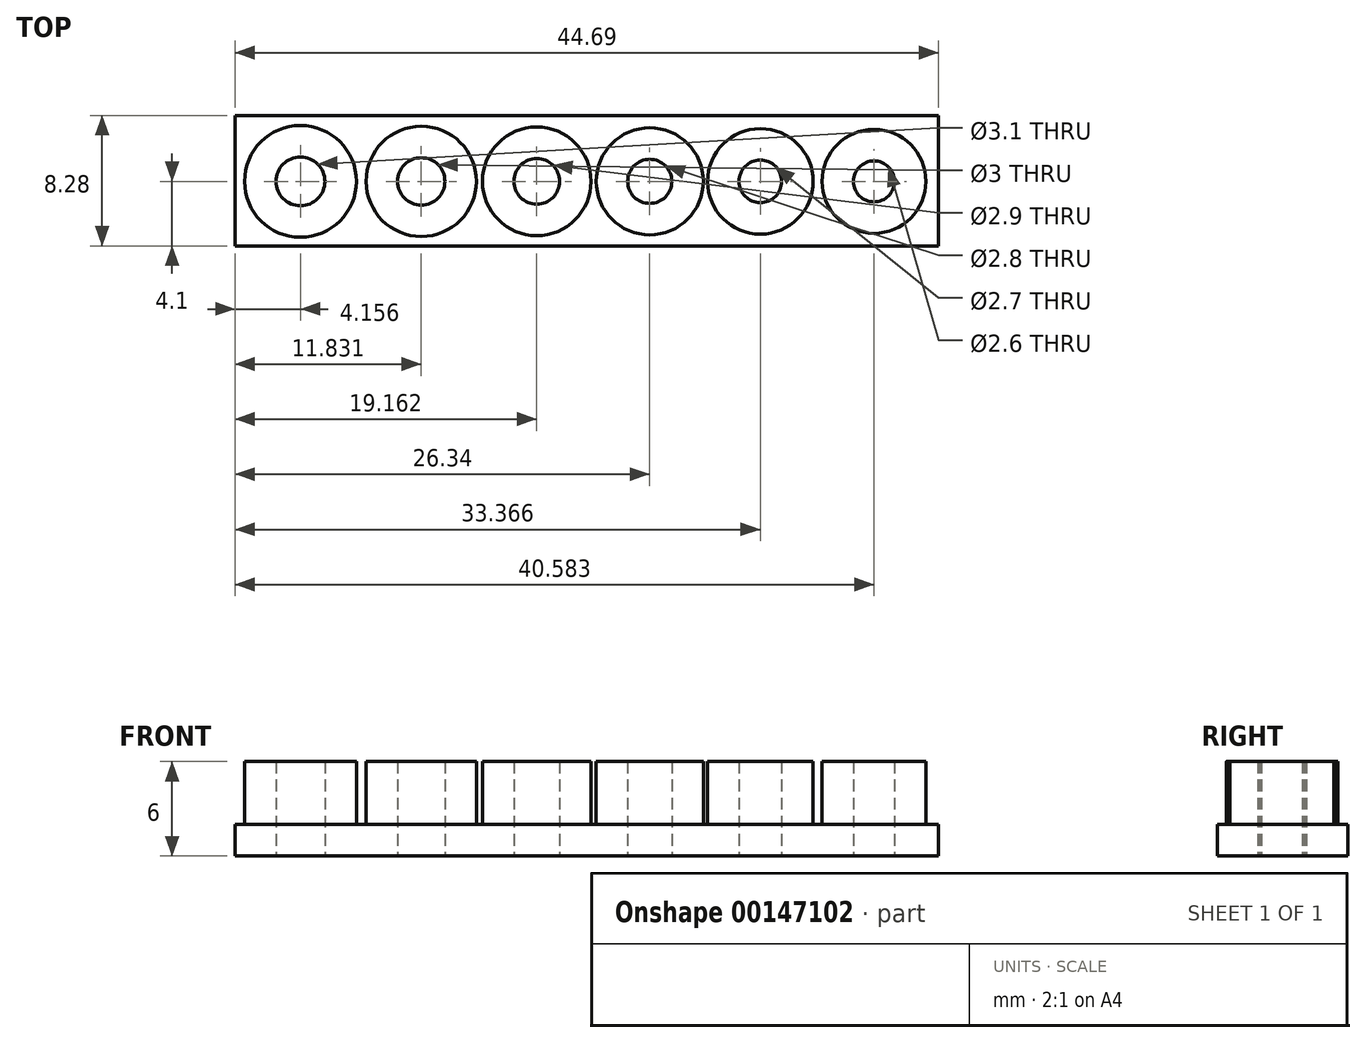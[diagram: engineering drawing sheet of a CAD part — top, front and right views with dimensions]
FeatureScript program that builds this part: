
annotation { "Feature Type Name" : "Feature", "Feature Type Description" : "" }
export const myFeature = defineFeature(function(context is Context, id is Id, definition is map)
    precondition{}
    {
        {
            var Q0;
            Q0=qCreatedBy(makeId("Top.planeOp"),FACE);
            var sketch = newSketch(context, id + "F0", { "sketchPlane" : qUnion([Q0])});
            skLineSegment(sketch, "E0", {"start": v(-20.66, -29) * mm, "end": v(15.04, -29) * mm, "construction": true});
            skCircle(sketch, "E1", {"center": v(-20.66, -29) * mm, "radius": 1.55 * mm});
            skCircle(sketch, "E2", {"center": v(-12.99, -29) * mm, "radius": 1.5 * mm});
            skCircle(sketch, "E3", {"center": v(-5.66, -29) * mm, "radius": 1.45 * mm});
            skCircle(sketch, "E4", {"center": v(1.52, -29) * mm, "radius": 1.4 * mm});
            skCircle(sketch, "E5", {"center": v(8.55, -29) * mm, "radius": 1.35 * mm});
            skCircle(sketch, "E6", {"center": v(15.76, -29) * mm, "radius": 1.3 * mm});
            skLineSegment(sketch, "E7.bottom", {"start": v(-24.82, -24.81) * mm, "end": v(19.87, -24.81) * mm});
            skLineSegment(sketch, "E7.top", {"start": v(-24.82, -33.1) * mm, "end": v(19.87, -33.1) * mm});
            skLineSegment(sketch, "E7.left", {"start": v(-24.82, -24.81) * mm, "end": v(-24.82, -33.1) * mm});
            skLineSegment(sketch, "E7.right", {"start": v(19.87, -24.81) * mm, "end": v(19.87, -33.1) * mm});
            skCircle(sketch, "E8", {"center": v(-20.66, -29) * mm, "radius": 3.55 * mm});
            skCircle(sketch, "E9", {"center": v(-12.99, -29) * mm, "radius": 3.5 * mm});
            skCircle(sketch, "E10", {"center": v(-5.66, -29) * mm, "radius": 3.45 * mm});
            skCircle(sketch, "E11", {"center": v(1.52, -29) * mm, "radius": 3.4 * mm});
            skCircle(sketch, "E12", {"center": v(8.55, -29) * mm, "radius": 3.35 * mm});
            skCircle(sketch, "E13", {"center": v(15.76, -29) * mm, "radius": 3.3 * mm});
            skSolve(sketch);
        }
        {
            var Q0;
            Q0=makeQuery(id+"F0.imprint","IMPRINT",FACE,{"disambiguationData":[TD([[makeQuery(id+"F0.imprint","IMPRINT",EDGE,{"derivedFrom":sQuery(id+"F0.wireOp",EDGE,"E7.bottom")}),-1.0]])]});
            extrude(context, id + "F1", {"entities" : qUnion([Q0]), "depth" : 2 * mm});
        }
        {
            var Q0;
            Q0=makeQuery(id+"F0.imprint","IMPRINT",FACE,{"disambiguationData":[TD([[makeQuery(id+"F0.imprint","IMPRINT",EDGE,{"derivedFrom":sQuery(id+"F0.wireOp",EDGE,"E1")}),-1.0]])]});
            var Q1;
            Q1=makeQuery(id+"F0.imprint","IMPRINT",FACE,{"disambiguationData":[TD([[makeQuery(id+"F0.imprint","IMPRINT",EDGE,{"derivedFrom":sQuery(id+"F0.wireOp",EDGE,"E2")}),-1.0]])]});
            var Q2;
            Q2=makeQuery(id+"F0.imprint","IMPRINT",FACE,{"disambiguationData":[TD([[makeQuery(id+"F0.imprint","IMPRINT",EDGE,{"derivedFrom":sQuery(id+"F0.wireOp",EDGE,"E3")}),-1.0]])]});
            var Q3;
            Q3=makeQuery(id+"F0.imprint","IMPRINT",FACE,{"disambiguationData":[TD([[makeQuery(id+"F0.imprint","IMPRINT",EDGE,{"derivedFrom":sQuery(id+"F0.wireOp",EDGE,"E4")}),-1.0]])]});
            var Q4;
            Q4=makeQuery(id+"F0.imprint","IMPRINT",FACE,{"disambiguationData":[TD([[makeQuery(id+"F0.imprint","IMPRINT",EDGE,{"derivedFrom":sQuery(id+"F0.wireOp",EDGE,"E5")}),-1.0]])]});
            var Q5;
            Q5=makeQuery(id+"F0.imprint","IMPRINT",FACE,{"disambiguationData":[TD([[makeQuery(id+"F0.imprint","IMPRINT",EDGE,{"derivedFrom":sQuery(id+"F0.wireOp",EDGE,"E6")}),-1.0]])]});
            extrude(context, id + "F2", {"entities" : qUnion([Q0, Q1, Q2, Q3, Q4, Q5]), "operationType" : NewBodyOperationType.ADD, "depth" : 6 * mm});
        }
    });
